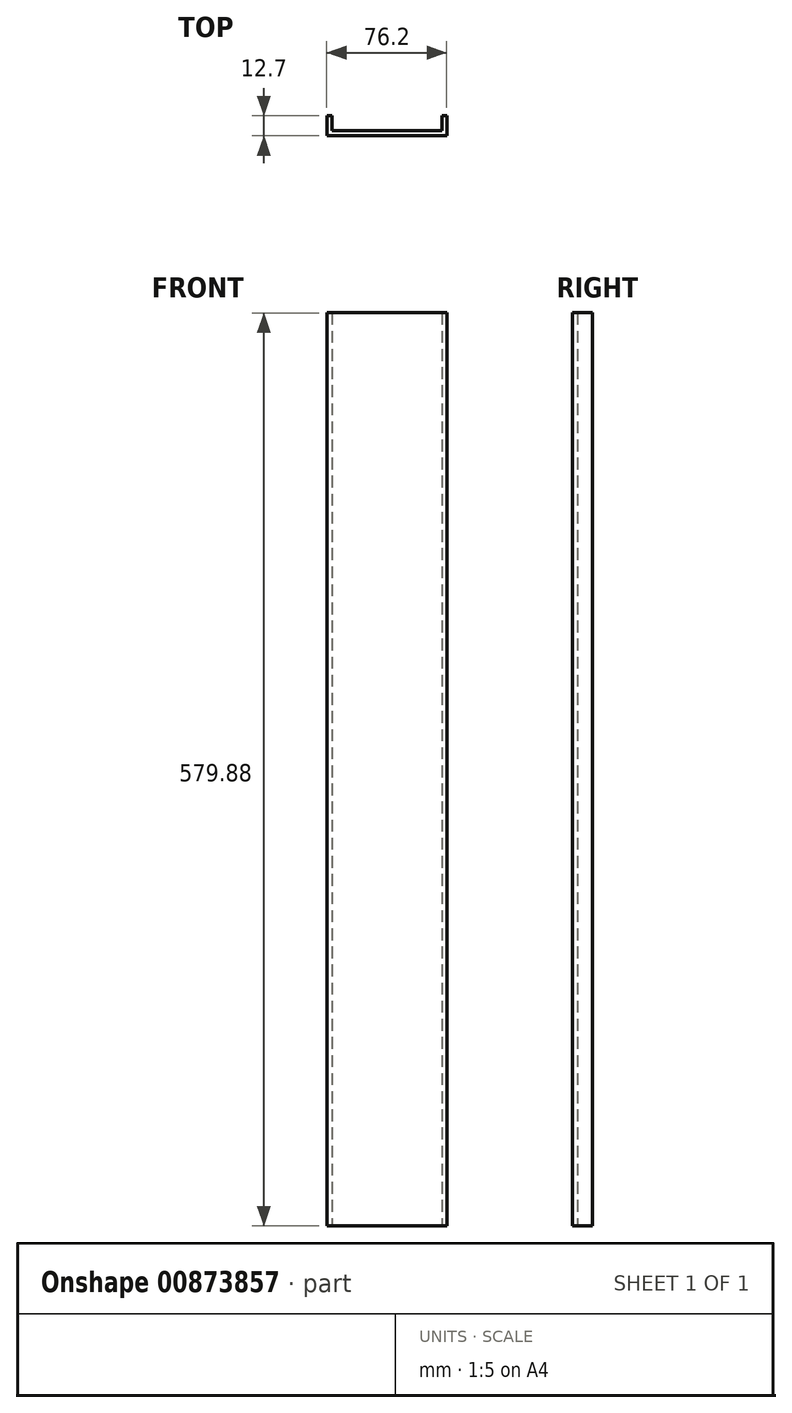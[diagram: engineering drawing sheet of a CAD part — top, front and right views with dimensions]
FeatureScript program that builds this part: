
annotation { "Feature Type Name" : "Feature", "Feature Type Description" : "" }
export const myFeature = defineFeature(function(context is Context, id is Id, definition is map)
    precondition{}
    {
        {
            var Q0;
            Q0=qCreatedBy(makeId("Top.planeOp"),FACE);
            var sketch = newSketch(context, id + "F0", { "sketchPlane" : qUnion([Q0])});
            skLineSegment(sketch, "E0", {"start": v(-21.53, 12.7) * mm, "end": v(-21.53, 0) * mm});
            skLineSegment(sketch, "E1", {"start": v(-21.53, 0) * mm, "end": v(54.67, 0) * mm});
            skLineSegment(sketch, "E2", {"start": v(54.67, 0) * mm, "end": v(54.67, 12.7) * mm});
            skLineSegment(sketch, "E3", {"start": v(54.67, 12.7) * mm, "end": v(51.5, 12.7) * mm});
            skLineSegment(sketch, "E4", {"start": v(51.5, 12.7) * mm, "end": v(51.5, 3.18) * mm});
            skLineSegment(sketch, "E5", {"start": v(51.5, 3.18) * mm, "end": v(-18.35, 3.17) * mm});
            skLineSegment(sketch, "E6", {"start": v(-18.35, 3.17) * mm, "end": v(-18.35, 12.7) * mm});
            skLineSegment(sketch, "E7", {"start": v(-18.35, 12.7) * mm, "end": v(-21.53, 12.7) * mm});
            skSolve(sketch);
        }
        {
            var Q0;
            Q0=makeQuery(id+"F0.imprint","IMPRINT",FACE,{"disambiguationData":[TD([[makeQuery(id+"F0.imprint","IMPRINT",EDGE,{"derivedFrom":sQuery(id+"F0.wireOp",EDGE,"E0")}),1.0]])]});
            extrude(context, id + "F1", {"entities" : qUnion([Q0]), "depth" : 579.88 * mm, "offsetDistance" : 25.4 * mm});
        }
    });
